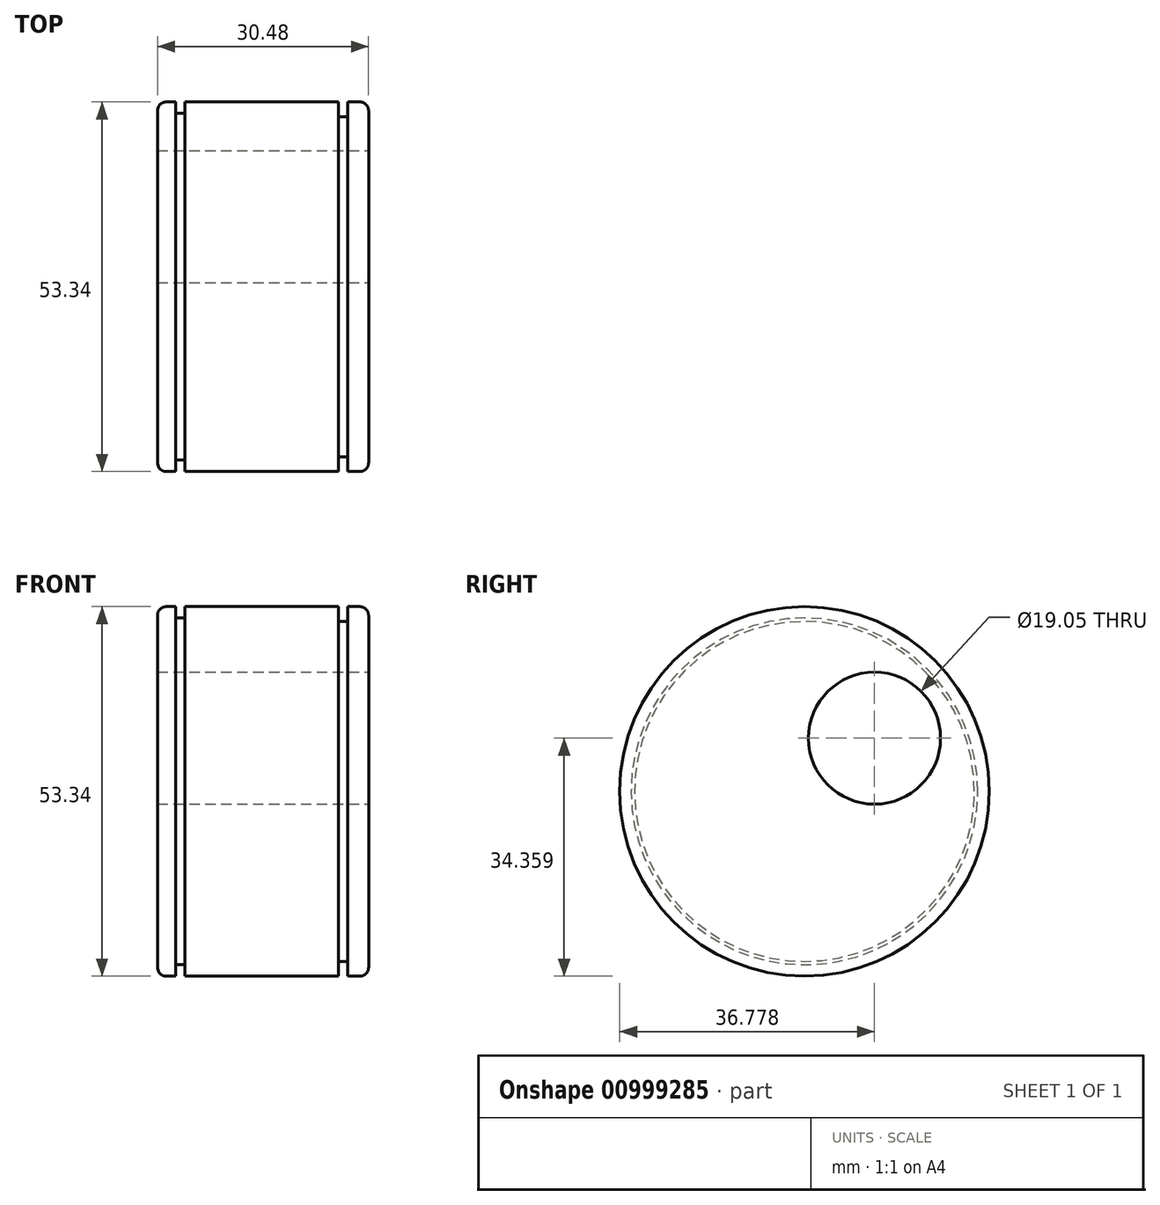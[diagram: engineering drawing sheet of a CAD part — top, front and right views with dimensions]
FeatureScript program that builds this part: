
annotation { "Feature Type Name" : "Feature", "Feature Type Description" : "" }
export const myFeature = defineFeature(function(context is Context, id is Id, definition is map)
    precondition{}
    {
        {
            var Q0;
            Q0=qCreatedBy(makeId("Front.planeOp"),FACE);
            var sketch = newSketch(context, id + "F0", { "sketchPlane" : qUnion([Q0])});
            skLineSegment(sketch, "E0", {"start": v(-25.47, 0) * mm, "end": v(26.15, 0) * mm, "construction": true});
            skLineSegment(sketch, "E1", {"start": v(-14.66, 0) * mm, "end": v(-14.66, 26.67) * mm});
            skLineSegment(sketch, "E2", {"start": v(-14.66, 26.67) * mm, "end": v(-12.03, 26.67) * mm});
            skLineSegment(sketch, "E3", {"start": v(-12.03, 26.67) * mm, "end": v(-12.03, 25.01) * mm});
            skLineSegment(sketch, "E4", {"start": v(-12.03, 25.01) * mm, "end": v(-10.66, 25.01) * mm});
            skLineSegment(sketch, "E5", {"start": v(-10.66, 25.01) * mm, "end": v(-10.66, 26.67) * mm});
            skLineSegment(sketch, "E6", {"start": v(-10.66, 26.67) * mm, "end": v(11.44, 26.67) * mm});
            skLineSegment(sketch, "E7", {"start": v(11.44, 26.67) * mm, "end": v(11.44, 24.53) * mm});
            skLineSegment(sketch, "E8", {"start": v(11.44, 24.53) * mm, "end": v(12.8, 24.53) * mm});
            skLineSegment(sketch, "E9", {"start": v(12.8, 24.53) * mm, "end": v(12.8, 26.67) * mm});
            skLineSegment(sketch, "E10", {"start": v(12.8, 26.67) * mm, "end": v(15.82, 26.67) * mm});
            skLineSegment(sketch, "E11", {"start": v(15.82, 26.67) * mm, "end": v(15.82, 0) * mm});
            skLineSegment(sketch, "E12", {"start": v(15.82, 0) * mm, "end": v(-14.66, 0) * mm});
            skLineSegment(sketch, "E13", {"start": v(-22.06, 26.67) * mm, "end": v(25.56, 26.67) * mm, "construction": true});
            skSolve(sketch);
        }
        {
            var Q0;
            Q0 = qSketchRegion(id + "F0", true);
            var Q1;
            Q1=sQuery(id+"F0.wireOp",EDGE,"E0");
            revolve(context, id + "F1", {"surfaceOperationType" : NewSurfaceOperationType.NEW, "entities" : qUnion([Q0]), "axis" : qUnion([Q1]), "revolveType" : RevolveType.FULL});
        }
        {
            var Q0;
            Q0=makeQuery(id+"F1.opRevolve","SWEPT_EDGE",EDGE,{"disambiguationData":[OSD([sQuery(id+"F0.wireOp",EDGE,"E1"),sQuery(id+"F0.wireOp",EDGE,"E2")])]});
            var Q1;
            Q1=makeQuery(id+"F1.opRevolve","SWEPT_EDGE",EDGE,{"disambiguationData":[OSD([sQuery(id+"F0.wireOp",EDGE,"E10"),sQuery(id+"F0.wireOp",EDGE,"E11")])]});
            fillet(context, id + "F2", {"entities" : qUnion([Q0, Q1]), "radius" : 1.27 * mm, "tangentPropagation" : true, "allowEdgeOverflow" : false});
        }
        {
            var Q0;
            Q0=makeQuery(id+"F1.opRevolve","SWEPT_FACE",FACE,{"disambiguationData":[OSD([sQuery(id+"F0.wireOp",EDGE,"E11")])]});
            var sketch = newSketch(context, id + "F3", { "sketchPlane" : qUnion([Q0])});
            skCircle(sketch, "E14", {"center": v(10.1, 7.69) * mm, "radius": 9.53 * mm});
            skCircle(sketch, "E15", {"center": v(0, 0) * mm, "radius": 12.7 * mm, "construction": true});
            skSolve(sketch);
        }
        {
            var Q0;
            Q0 = qSketchRegion(id + "F3", true);
            extrude(context, id + "F4", {"entities" : qUnion([Q0]), "operationType" : NewBodyOperationType.REMOVE, "endBound" : BoundingType.THROUGH_ALL, "oppositeDirection" : true, "depth" : 25.4 * mm, "offsetDistance" : 25.4 * mm});
        }
    });
